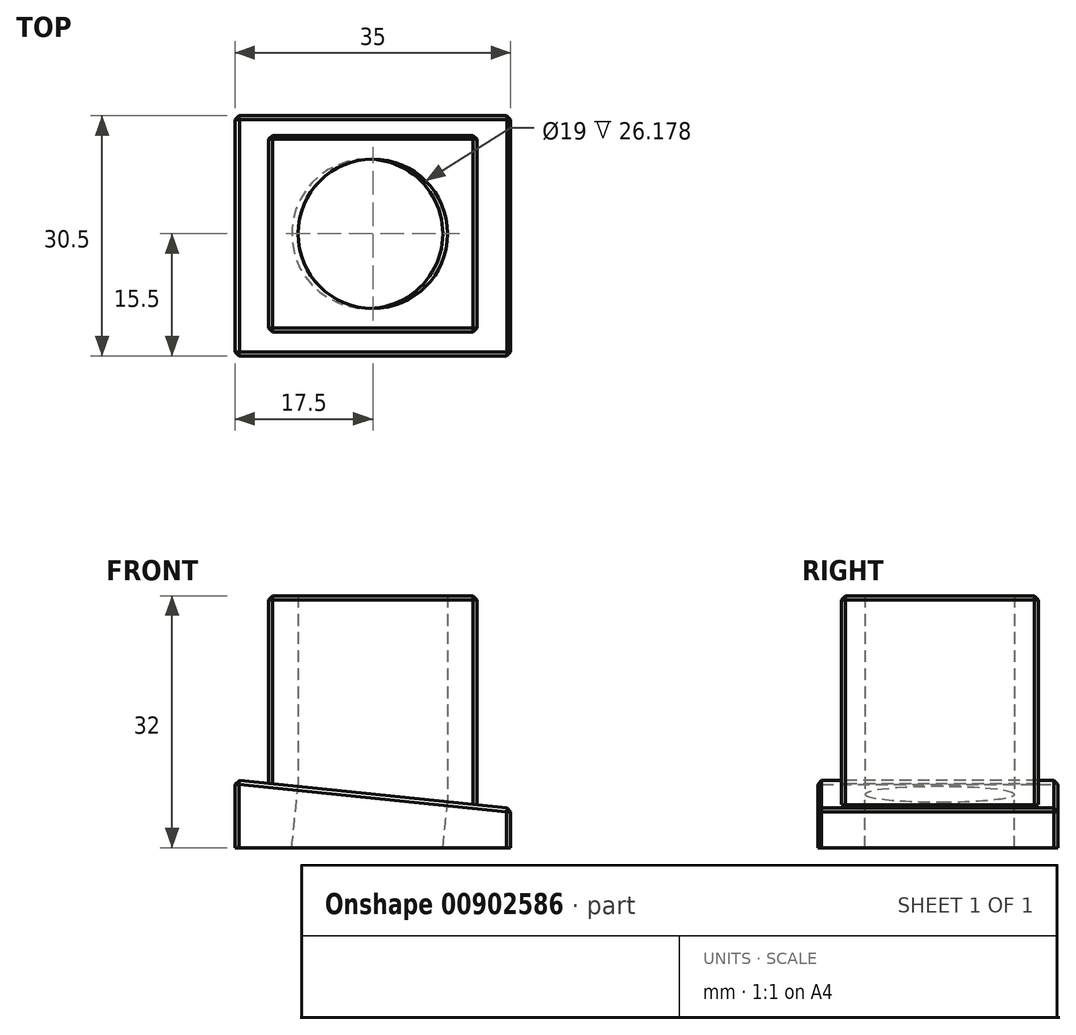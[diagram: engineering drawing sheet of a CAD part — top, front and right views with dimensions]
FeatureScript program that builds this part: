
annotation { "Feature Type Name" : "Feature", "Feature Type Description" : "" }
export const myFeature = defineFeature(function(context is Context, id is Id, definition is map)
    precondition{}
    {
        {
            var Q0;
            Q0=qCreatedBy(makeId("Top.planeOp"),FACE);
            var sketch = newSketch(context, id + "F0", { "sketchPlane" : qUnion([Q0])});
            skLineSegment(sketch, "E0.bottom", {"start": v(-13.25, 0) * mm, "end": v(13.25, 0) * mm});
            skLineSegment(sketch, "E0.top", {"start": v(-13.25, -25) * mm, "end": v(13.25, -25) * mm});
            skLineSegment(sketch, "E0.left", {"start": v(-13.25, 0) * mm, "end": v(-13.25, -25) * mm});
            skLineSegment(sketch, "E0.right", {"start": v(13.25, 0) * mm, "end": v(13.25, -25) * mm});
            skCircle(sketch, "E1", {"center": v(0, -12.5) * mm, "radius": 9.5 * mm});
            skPoint(sketch, "E1.centerSnap0", {"position": v(13.25, -12.5) * mm});
            skLineSegment(sketch, "E2.bottom", {"start": v(-17.5, 2.75) * mm, "end": v(17.5, 2.75) * mm});
            skLineSegment(sketch, "E2.top", {"start": v(-17.5, -27.75) * mm, "end": v(17.5, -27.75) * mm});
            skLineSegment(sketch, "E2.left", {"start": v(-17.5, 2.75) * mm, "end": v(-17.5, -27.75) * mm});
            skLineSegment(sketch, "E2.right", {"start": v(17.5, 2.75) * mm, "end": v(17.5, -27.75) * mm});
            skSolve(sketch);
        }
        {
            var Q0;
            Q0=qCreatedBy(makeId("Front.planeOp"),FACE);
            var sketch = newSketch(context, id + "F1", { "sketchPlane" : qUnion([Q0])});
            skLineSegment(sketch, "E3", {"start": v(-17.5, 0) * mm, "end": v(-17.5, 8.6) * mm});
            skLineSegment(sketch, "E4", {"start": v(17.5, 0) * mm, "end": v(17.5, 5) * mm});
            skLineSegment(sketch, "E5", {"start": v(-17.5, 8.6) * mm, "end": v(17.5, 5) * mm});
            skLineSegment(sketch, "E6", {"start": v(17.5, 0) * mm, "end": v(-17.5, 0) * mm});
            skSolve(sketch);
        }
        {
            var Q0;
            Q0 = qSketchRegion(id + "F1", true);
            extrude(context, id + "F2", {"entities" : qUnion([Q0]), "depth" : 28 * mm, "offsetDistance" : 25 * mm});
        }
        {
            var Q0;
            Q0 = qSketchRegion(id + "F1", true);
            extrude(context, id + "F3", {"entities" : qUnion([Q0]), "operationType" : NewBodyOperationType.ADD, "oppositeDirection" : true, "depth" : 2.5 * mm, "offsetDistance" : 25 * mm});
        }
        {
            var Q0;
            Q0=makeQuery(id+"F0.imprint","IMPRINT",FACE,{"disambiguationData":[TD([[makeQuery(id+"F0.imprint","IMPRINT",EDGE,{"derivedFrom":sQuery(id+"F0.wireOp",EDGE,"E0.bottom")}),-1.0]])]});
            extrude(context, id + "F4", {"entities" : qUnion([Q0]), "operationType" : NewBodyOperationType.ADD, "depth" : 32 * mm, "offsetDistance" : 25 * mm});
        }
        {
            var Q0;
            Q0=makeQuery(id+"F4.opExtrude","CAP_EDGE",EDGE,{"disambiguationData":[OSD([sQuery(id+"F0.wireOp",EDGE,"E0.left")])],"isStart":false});
            var Q1;
            Q1=makeQuery(id+"F4.opExtrude","CAP_EDGE",EDGE,{"disambiguationData":[OSD([sQuery(id+"F0.wireOp",EDGE,"E0.top")])],"isStart":false});
            var Q2;
            Q2=makeQuery(id+"F4.opExtrude","SWEPT_EDGE",EDGE,{"disambiguationData":[OSD([sQuery(id+"F0.wireOp",EDGE,"E0.bottom"),sQuery(id+"F0.wireOp",EDGE,"E0.right")])]});
            var Q3;
            Q3=makeQuery(id+"F4.opExtrude","CAP_EDGE",EDGE,{"disambiguationData":[OSD([sQuery(id+"F0.wireOp",EDGE,"E0.right")])],"isStart":false});
            var Q4;
            Q4=makeQuery(id+"F4.opExtrude","CAP_EDGE",EDGE,{"disambiguationData":[OSD([sQuery(id+"F0.wireOp",EDGE,"E0.bottom")])],"isStart":false});
            var Q5;
            Q5=makeQuery(id+"F4.opExtrude","SWEPT_EDGE",EDGE,{"disambiguationData":[OSD([sQuery(id+"F0.wireOp",EDGE,"E0.top"),sQuery(id+"F0.wireOp",EDGE,"E0.right")])]});
            var Q6;
            Q6=makeQuery(id+"F4.opExtrude","SWEPT_EDGE",EDGE,{"disambiguationData":[OSD([sQuery(id+"F0.wireOp",EDGE,"E0.top"),sQuery(id+"F0.wireOp",EDGE,"E0.left")])]});
            var Q7;
            Q7=makeQuery(id+"F4.opExtrude","SWEPT_EDGE",EDGE,{"disambiguationData":[OSD([sQuery(id+"F0.wireOp",EDGE,"E0.bottom"),sQuery(id+"F0.wireOp",EDGE,"E0.left")])]});
            var Q8;
            {var subQ0=sQuery(id+"F1.wireOp",EDGE,"E5");var subQ1=sQuery(id+"F1.wireOp",EDGE,"E3");Q8=makeQuery(id+"F3.boolean.opBoolean","MERGE",EDGE,{"derivedFrom":[makeQuery(id+"F2.opExtrude","SWEPT_EDGE",EDGE,{"disambiguationData":[OSD([subQ1,subQ0])]}),makeQuery(id+"F3.opExtrude","SWEPT_EDGE",EDGE,{"disambiguationData":[OSD([subQ1,subQ0])]})]});}
            var Q9;
            Q9=makeQuery(id+"F3.opExtrude","CAP_EDGE",EDGE,{"disambiguationData":[OSD([sQuery(id+"F1.wireOp",EDGE,"E5")])],"isStart":false});
            var Q10;
            {var subQ0=sQuery(id+"F1.wireOp",EDGE,"E5");var subQ1=sQuery(id+"F1.wireOp",EDGE,"E4");Q10=makeQuery(id+"F3.boolean.opBoolean","MERGE",EDGE,{"derivedFrom":[makeQuery(id+"F2.opExtrude","SWEPT_EDGE",EDGE,{"disambiguationData":[OSD([subQ1,subQ0])]}),makeQuery(id+"F3.opExtrude","SWEPT_EDGE",EDGE,{"disambiguationData":[OSD([subQ1,subQ0])]})]});}
            var Q11;
            Q11=makeQuery(id+"F2.opExtrude","CAP_EDGE",EDGE,{"disambiguationData":[OSD([sQuery(id+"F1.wireOp",EDGE,"E5")])],"isStart":false});
            var Q12;
            Q12=makeQuery(id+"F2.opExtrude","CAP_EDGE",EDGE,{"disambiguationData":[OSD([sQuery(id+"F1.wireOp",EDGE,"E3")])],"isStart":false});
            var Q13;
            Q13=makeQuery(id+"F2.opExtrude","CAP_EDGE",EDGE,{"disambiguationData":[OSD([sQuery(id+"F1.wireOp",EDGE,"E4")])],"isStart":false});
            var Q14;
            Q14=makeQuery(id+"F3.opExtrude","CAP_EDGE",EDGE,{"disambiguationData":[OSD([sQuery(id+"F1.wireOp",EDGE,"E3")])],"isStart":false});
            var Q15;
            Q15=makeQuery(id+"F3.opExtrude","CAP_EDGE",EDGE,{"disambiguationData":[OSD([sQuery(id+"F1.wireOp",EDGE,"E4")])],"isStart":false});
            chamfer(context, id + "F5", {"entities" : qUnion([Q0, Q1, Q2, Q3, Q4, Q5, Q6, Q7, Q8, Q9, Q10, Q11, Q12, Q13, Q14, Q15]), "width" : 0.5 * mm, "tangentPropagation" : true});
        }
        {
            var Q0;
            {var subQ0=sQuery(id+"F1.wireOp",EDGE,"E5");Q0=makeQuery(id+"F4.boolean.opBoolean","SPLIT",FACE,{"disambiguationData":[TD([makeQuery(id+"F4.opExtrude","SWEPT_FACE",FACE,{"disambiguationData":[OSD([sQuery(id+"F0.wireOp",EDGE,"E1")])]})])],"derivedFrom":makeQuery(id+"F3.boolean.opBoolean","MERGE",FACE,{"derivedFrom":[makeQuery(id+"F2.opExtrude","SWEPT_FACE",FACE,{"disambiguationData":[OSD([subQ0])]}),makeQuery(id+"F3.opExtrude","SWEPT_FACE",FACE,{"disambiguationData":[OSD([subQ0])]})]})});}
            extrude(context, id + "F6", {"entities" : qUnion([Q0]), "operationType" : NewBodyOperationType.REMOVE, "oppositeDirection" : true, "depth" : 25 * mm, "offsetDistance" : 25 * mm});
        }
    });
